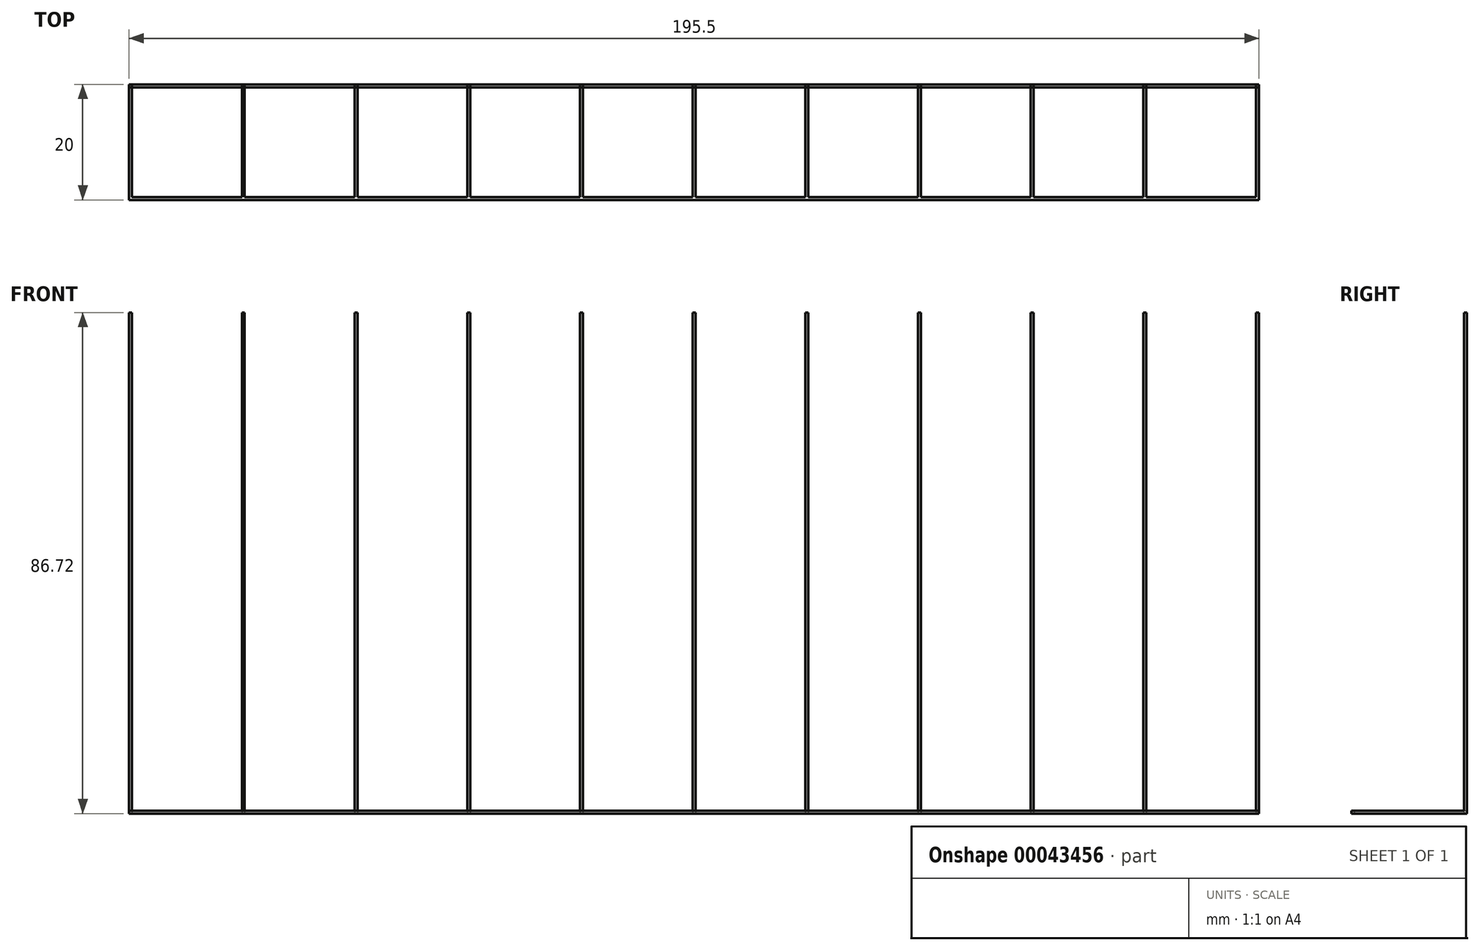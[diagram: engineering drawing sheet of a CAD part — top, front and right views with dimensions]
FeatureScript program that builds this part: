
annotation { "Feature Type Name" : "Feature", "Feature Type Description" : "" }
export const myFeature = defineFeature(function(context is Context, id is Id, definition is map)
    precondition{}
    {
        {
            var Q0;
            Q0=qCreatedBy(makeId("Top.planeOp"),FACE);
            var sketch = newSketch(context, id + "F0", { "sketchPlane" : qUnion([Q0])});
            skLineSegment(sketch, "E0.left", {"start": v(-64.95, 61.53) * mm, "end": v(-64.95, 41.53) * mm});
            skLineSegment(sketch, "E0.right", {"start": v(-44.95, 61.03) * mm, "end": v(-44.95, 42.03) * mm});
            skLineSegment(sketch, "E1.0", {"start": v(-64.45, 61.03) * mm, "end": v(-45.45, 61.03) * mm});
            skLineSegment(sketch, "E1.1", {"start": v(-64.45, 61.03) * mm, "end": v(-64.45, 42.03) * mm});
            skLineSegment(sketch, "E1.2", {"start": v(-64.45, 42.03) * mm, "end": v(-45.45, 42.03) * mm});
            skLineSegment(sketch, "E1.3", {"start": v(-45.45, 61.03) * mm, "end": v(-45.45, 42.03) * mm});
            skLineSegment(sketch, "E2.1.0.1", {"start": v(-44.95, 61.03) * mm, "end": v(-25.95, 61.03) * mm});
            skLineSegment(sketch, "E2.1.0.4", {"start": v(-44.95, 42.03) * mm, "end": v(-25.95, 42.03) * mm});
            skLineSegment(sketch, "E2.1.0.6", {"start": v(-25.95, 61.03) * mm, "end": v(-25.95, 42.03) * mm});
            skLineSegment(sketch, "E2.1.0.7", {"start": v(-25.45, 61.03) * mm, "end": v(-25.45, 42.03) * mm});
            skLineSegment(sketch, "E2.2.0.1", {"start": v(-25.45, 61.03) * mm, "end": v(-6.45, 61.03) * mm});
            skLineSegment(sketch, "E2.2.0.3", {"start": v(-25.45, 61.03) * mm, "end": v(-25.45, 42.03) * mm});
            skLineSegment(sketch, "E2.2.0.4", {"start": v(-25.45, 42.03) * mm, "end": v(-6.45, 42.03) * mm});
            skLineSegment(sketch, "E2.2.0.6", {"start": v(-6.45, 61.03) * mm, "end": v(-6.45, 42.03) * mm});
            skLineSegment(sketch, "E2.2.0.7", {"start": v(-5.95, 61.03) * mm, "end": v(-5.95, 42.03) * mm});
            skLineSegment(sketch, "E2.3.0.1", {"start": v(-5.95, 61.03) * mm, "end": v(13.05, 61.03) * mm});
            skLineSegment(sketch, "E2.3.0.2", {"start": v(-6.45, 61.03) * mm, "end": v(-6.45, 42.03) * mm});
            skLineSegment(sketch, "E2.3.0.3", {"start": v(-5.95, 61.03) * mm, "end": v(-5.95, 42.03) * mm});
            skLineSegment(sketch, "E2.3.0.4", {"start": v(-5.95, 42.03) * mm, "end": v(13.05, 42.03) * mm});
            skLineSegment(sketch, "E2.3.0.6", {"start": v(13.05, 61.03) * mm, "end": v(13.05, 42.03) * mm});
            skLineSegment(sketch, "E2.3.0.7", {"start": v(13.55, 61.03) * mm, "end": v(13.55, 42.03) * mm});
            skLineSegment(sketch, "E2.4.0.1", {"start": v(13.55, 61.03) * mm, "end": v(32.55, 61.03) * mm});
            skLineSegment(sketch, "E2.4.0.2", {"start": v(13.05, 61.03) * mm, "end": v(13.05, 42.03) * mm});
            skLineSegment(sketch, "E2.4.0.3", {"start": v(13.55, 61.03) * mm, "end": v(13.55, 42.03) * mm});
            skLineSegment(sketch, "E2.4.0.4", {"start": v(13.55, 42.03) * mm, "end": v(32.55, 42.03) * mm});
            skLineSegment(sketch, "E2.4.0.6", {"start": v(32.55, 61.03) * mm, "end": v(32.55, 42.03) * mm});
            skLineSegment(sketch, "E2.4.0.7", {"start": v(33.05, 61.03) * mm, "end": v(33.05, 42.03) * mm});
            skLineSegment(sketch, "E2.5.0.1", {"start": v(33.05, 61.03) * mm, "end": v(52.05, 61.03) * mm});
            skLineSegment(sketch, "E2.5.0.2", {"start": v(32.55, 61.03) * mm, "end": v(32.55, 42.03) * mm});
            skLineSegment(sketch, "E2.5.0.3", {"start": v(33.05, 61.03) * mm, "end": v(33.05, 42.03) * mm});
            skLineSegment(sketch, "E2.5.0.4", {"start": v(33.05, 42.03) * mm, "end": v(52.05, 42.03) * mm});
            skLineSegment(sketch, "E2.5.0.6", {"start": v(52.05, 61.03) * mm, "end": v(52.05, 42.03) * mm});
            skLineSegment(sketch, "E2.5.0.7", {"start": v(52.55, 61.03) * mm, "end": v(52.55, 42.03) * mm});
            skLineSegment(sketch, "E2.6.0.1", {"start": v(52.55, 61.03) * mm, "end": v(71.55, 61.03) * mm});
            skLineSegment(sketch, "E2.6.0.3", {"start": v(52.55, 61.03) * mm, "end": v(52.55, 42.03) * mm});
            skLineSegment(sketch, "E2.6.0.4", {"start": v(52.55, 42.03) * mm, "end": v(71.55, 42.03) * mm});
            skLineSegment(sketch, "E2.6.0.6", {"start": v(71.55, 61.03) * mm, "end": v(71.55, 42.03) * mm});
            skLineSegment(sketch, "E2.6.0.7", {"start": v(72.05, 61.03) * mm, "end": v(72.05, 42.03) * mm});
            skLineSegment(sketch, "E2.7.0.1", {"start": v(72.05, 61.03) * mm, "end": v(91.05, 61.03) * mm});
            skLineSegment(sketch, "E2.7.0.2", {"start": v(71.55, 61.03) * mm, "end": v(71.55, 42.03) * mm});
            skLineSegment(sketch, "E2.7.0.3", {"start": v(72.05, 61.03) * mm, "end": v(72.05, 42.03) * mm});
            skLineSegment(sketch, "E2.7.0.4", {"start": v(72.05, 42.03) * mm, "end": v(91.05, 42.03) * mm});
            skLineSegment(sketch, "E2.7.0.6", {"start": v(91.05, 61.03) * mm, "end": v(91.05, 42.03) * mm});
            skLineSegment(sketch, "E2.8.0.1", {"start": v(91.55, 61.03) * mm, "end": v(110.55, 61.03) * mm});
            skLineSegment(sketch, "E2.8.0.2", {"start": v(91.05, 61.03) * mm, "end": v(91.05, 42.03) * mm});
            skLineSegment(sketch, "E2.8.0.3", {"start": v(91.55, 61.03) * mm, "end": v(91.55, 42.03) * mm});
            skLineSegment(sketch, "E2.8.0.4", {"start": v(91.55, 42.03) * mm, "end": v(110.55, 42.03) * mm});
            skLineSegment(sketch, "E2.8.0.6", {"start": v(110.55, 61.03) * mm, "end": v(110.55, 42.03) * mm});
            skLineSegment(sketch, "E2.8.0.7", {"start": v(111.05, 61.03) * mm, "end": v(111.05, 42.03) * mm});
            skLineSegment(sketch, "E2.9.0.1", {"start": v(111.05, 61.03) * mm, "end": v(130.05, 61.03) * mm});
            skLineSegment(sketch, "E2.9.0.2", {"start": v(110.55, 61.03) * mm, "end": v(110.55, 42.03) * mm});
            skLineSegment(sketch, "E2.9.0.3", {"start": v(111.05, 61.03) * mm, "end": v(111.05, 42.03) * mm});
            skLineSegment(sketch, "E2.9.0.4", {"start": v(111.05, 42.03) * mm, "end": v(130.05, 42.03) * mm});
            skLineSegment(sketch, "E2.9.0.6", {"start": v(130.05, 61.03) * mm, "end": v(130.05, 42.03) * mm});
            skLineSegment(sketch, "E2.9.0.7", {"start": v(130.55, 61.53) * mm, "end": v(130.55, 41.53) * mm});
            skPoint(sketch, "E3.orphan", {"position": v(32.55, 61.53) * mm});
            skPoint(sketch, "E4.orphan", {"position": v(13.55, 61.53) * mm});
            skPoint(sketch, "E5.orphan", {"position": v(52.55, 61.53) * mm});
            skPoint(sketch, "E6.orphan", {"position": v(91.55, 41.53) * mm});
            skPoint(sketch, "E7.orphan", {"position": v(71.55, 41.53) * mm});
            skPoint(sketch, "E8.orphan", {"position": v(72.05, 41.53) * mm});
            skPoint(sketch, "E9.orphan", {"position": v(33.05, 41.53) * mm});
            skPoint(sketch, "E10.orphan", {"position": v(-5.95, 41.53) * mm});
            skLineSegment(sketch, "E11", {"start": v(130.55, 61.53) * mm, "end": v(-64.95, 61.53) * mm});
            skLineSegment(sketch, "E12", {"start": v(-64.95, 41.53) * mm, "end": v(130.55, 41.53) * mm});
            skSolve(sketch);
        }
        {
            var Q0;
            Q0=makeQuery(id+"F0.imprint","IMPRINT",FACE,{"disambiguationData":[TD([[makeQuery(id+"F0.imprint","IMPRINT",EDGE,{"derivedFrom":sQuery(id+"F0.wireOp",EDGE,"E0.left")}),1.0]])]});
            extrude(context, id + "F1", {"entities" : qUnion([Q0]), "depth" : 0.5 * mm});
        }
        {
            var Q0;
            Q0=makeQuery(id+"F1.opExtrude","CAP_FACE",FACE,{"disambiguationData":[OSD([sQuery(id+"F0.wireOp",EDGE,"E0.left"),sQuery(id+"F0.wireOp",EDGE,"E1.0"),sQuery(id+"F0.wireOp",EDGE,"E1.1"),sQuery(id+"F0.wireOp",EDGE,"E1.2"),sQuery(id+"F0.wireOp",EDGE,"E2.1.0.1"),sQuery(id+"F0.wireOp",EDGE,"E1.3"),sQuery(id+"F0.wireOp",EDGE,"E0.right"),sQuery(id+"F0.wireOp",EDGE,"E2.1.0.4"),sQuery(id+"F0.wireOp",EDGE,"E2.1.0.6"),sQuery(id+"F0.wireOp",EDGE,"E2.2.0.1"),sQuery(id+"F0.wireOp",EDGE,"E2.2.0.3"),sQuery(id+"F0.wireOp",EDGE,"E2.2.0.4"),sQuery(id+"F0.wireOp",EDGE,"E2.3.0.1"),sQuery(id+"F0.wireOp",EDGE,"E2.3.0.2"),sQuery(id+"F0.wireOp",EDGE,"E2.3.0.3"),sQuery(id+"F0.wireOp",EDGE,"E2.3.0.4"),sQuery(id+"F0.wireOp",EDGE,"E2.4.0.1"),sQuery(id+"F0.wireOp",EDGE,"E2.4.0.2"),sQuery(id+"F0.wireOp",EDGE,"E2.4.0.3"),sQuery(id+"F0.wireOp",EDGE,"E2.4.0.4"),sQuery(id+"F0.wireOp",EDGE,"E2.5.0.1"),sQuery(id+"F0.wireOp",EDGE,"E2.5.0.2"),sQuery(id+"F0.wireOp",EDGE,"E2.5.0.3"),sQuery(id+"F0.wireOp",EDGE,"E2.5.0.4"),sQuery(id+"F0.wireOp",EDGE,"E2.5.0.6"),sQuery(id+"F0.wireOp",EDGE,"E2.6.0.1"),sQuery(id+"F0.wireOp",EDGE,"E2.6.0.3"),sQuery(id+"F0.wireOp",EDGE,"E2.6.0.4"),sQuery(id+"F0.wireOp",EDGE,"E2.7.0.1"),sQuery(id+"F0.wireOp",EDGE,"E2.7.0.2"),sQuery(id+"F0.wireOp",EDGE,"E2.7.0.3"),sQuery(id+"F0.wireOp",EDGE,"E2.7.0.4"),sQuery(id+"F0.wireOp",EDGE,"E2.8.0.1"),sQuery(id+"F0.wireOp",EDGE,"E2.8.0.2"),sQuery(id+"F0.wireOp",EDGE,"E2.8.0.3"),sQuery(id+"F0.wireOp",EDGE,"E2.8.0.4"),sQuery(id+"F0.wireOp",EDGE,"E2.9.0.1"),sQuery(id+"F0.wireOp",EDGE,"E2.9.0.2"),sQuery(id+"F0.wireOp",EDGE,"E2.9.0.3"),sQuery(id+"F0.wireOp",EDGE,"E2.9.0.4"),sQuery(id+"F0.wireOp",EDGE,"E2.9.0.6"),sQuery(id+"F0.wireOp",EDGE,"E2.9.0.7"),sQuery(id+"F0.wireOp",EDGE,"E11"),sQuery(id+"F0.wireOp",EDGE,"E12")])],"isStart":false});
            var sketch = newSketch(context, id + "F2", { "sketchPlane" : qUnion([Q0])});
            skLineSegment(sketch, "E13.bottom", {"start": v(-64.95, 61.53) * mm, "end": v(-64.45, 61.53) * mm});
            skLineSegment(sketch, "E13.top", {"start": v(-64.95, 61.03) * mm, "end": v(-64.45, 61.03) * mm});
            skLineSegment(sketch, "E13.left", {"start": v(-64.95, 61.53) * mm, "end": v(-64.95, 61.03) * mm});
            skLineSegment(sketch, "E13.right", {"start": v(-64.45, 61.53) * mm, "end": v(-64.45, 61.03) * mm});
            skLineSegment(sketch, "E14.bottom", {"start": v(-44.95, 61.03) * mm, "end": v(-45.45, 61.03) * mm});
            skLineSegment(sketch, "E14.top", {"start": v(-44.95, 61.53) * mm, "end": v(-45.45, 61.53) * mm});
            skLineSegment(sketch, "E14.left", {"start": v(-44.95, 61.03) * mm, "end": v(-44.95, 61.53) * mm});
            skLineSegment(sketch, "E14.right", {"start": v(-45.45, 61.03) * mm, "end": v(-45.45, 61.53) * mm});
            skLineSegment(sketch, "E15.bottom", {"start": v(-25.45, 61.03) * mm, "end": v(-25.95, 61.03) * mm});
            skLineSegment(sketch, "E15.top", {"start": v(-25.45, 61.53) * mm, "end": v(-25.95, 61.53) * mm});
            skLineSegment(sketch, "E15.left", {"start": v(-25.45, 61.03) * mm, "end": v(-25.45, 61.53) * mm});
            skLineSegment(sketch, "E15.right", {"start": v(-25.95, 61.03) * mm, "end": v(-25.95, 61.53) * mm});
            skLineSegment(sketch, "E16.bottom", {"start": v(-5.95, 61.03) * mm, "end": v(-6.45, 61.03) * mm});
            skLineSegment(sketch, "E16.top", {"start": v(-5.95, 61.53) * mm, "end": v(-6.45, 61.53) * mm});
            skLineSegment(sketch, "E16.left", {"start": v(-5.95, 61.03) * mm, "end": v(-5.95, 61.53) * mm});
            skLineSegment(sketch, "E16.right", {"start": v(-6.45, 61.03) * mm, "end": v(-6.45, 61.53) * mm});
            skLineSegment(sketch, "E17.bottom", {"start": v(13.55, 61.03) * mm, "end": v(13.05, 61.03) * mm});
            skLineSegment(sketch, "E17.top", {"start": v(13.55, 61.53) * mm, "end": v(13.05, 61.53) * mm});
            skLineSegment(sketch, "E17.left", {"start": v(13.55, 61.03) * mm, "end": v(13.55, 61.53) * mm});
            skLineSegment(sketch, "E17.right", {"start": v(13.05, 61.03) * mm, "end": v(13.05, 61.53) * mm});
            skLineSegment(sketch, "E18.bottom", {"start": v(33.05, 61.03) * mm, "end": v(32.55, 61.03) * mm});
            skLineSegment(sketch, "E18.top", {"start": v(33.05, 61.53) * mm, "end": v(32.55, 61.53) * mm});
            skLineSegment(sketch, "E18.left", {"start": v(33.05, 61.03) * mm, "end": v(33.05, 61.53) * mm});
            skLineSegment(sketch, "E18.right", {"start": v(32.55, 61.03) * mm, "end": v(32.55, 61.53) * mm});
            skLineSegment(sketch, "E19.bottom", {"start": v(52.55, 61.03) * mm, "end": v(52.05, 61.03) * mm});
            skLineSegment(sketch, "E19.top", {"start": v(52.55, 61.53) * mm, "end": v(52.05, 61.53) * mm});
            skLineSegment(sketch, "E19.left", {"start": v(52.55, 61.03) * mm, "end": v(52.55, 61.53) * mm});
            skLineSegment(sketch, "E19.right", {"start": v(52.05, 61.03) * mm, "end": v(52.05, 61.53) * mm});
            skLineSegment(sketch, "E20.bottom", {"start": v(72.05, 61.03) * mm, "end": v(71.55, 61.03) * mm});
            skLineSegment(sketch, "E20.top", {"start": v(72.05, 61.53) * mm, "end": v(71.55, 61.53) * mm});
            skLineSegment(sketch, "E20.left", {"start": v(72.05, 61.03) * mm, "end": v(72.05, 61.53) * mm});
            skLineSegment(sketch, "E20.right", {"start": v(71.55, 61.03) * mm, "end": v(71.55, 61.53) * mm});
            skLineSegment(sketch, "E21.bottom", {"start": v(91.55, 61.03) * mm, "end": v(91.05, 61.03) * mm});
            skLineSegment(sketch, "E21.top", {"start": v(91.55, 61.53) * mm, "end": v(91.05, 61.53) * mm});
            skLineSegment(sketch, "E21.left", {"start": v(91.55, 61.03) * mm, "end": v(91.55, 61.53) * mm});
            skLineSegment(sketch, "E21.right", {"start": v(91.05, 61.03) * mm, "end": v(91.05, 61.53) * mm});
            skLineSegment(sketch, "E22.bottom", {"start": v(111.05, 61.03) * mm, "end": v(110.55, 61.03) * mm});
            skLineSegment(sketch, "E22.top", {"start": v(111.05, 61.53) * mm, "end": v(110.55, 61.53) * mm});
            skLineSegment(sketch, "E22.left", {"start": v(111.05, 61.03) * mm, "end": v(111.05, 61.53) * mm});
            skLineSegment(sketch, "E22.right", {"start": v(110.55, 61.03) * mm, "end": v(110.55, 61.53) * mm});
            skLineSegment(sketch, "E23.bottom", {"start": v(130.05, 61.03) * mm, "end": v(130.55, 61.03) * mm});
            skLineSegment(sketch, "E23.top", {"start": v(130.05, 61.53) * mm, "end": v(130.55, 61.53) * mm});
            skLineSegment(sketch, "E23.left", {"start": v(130.05, 61.03) * mm, "end": v(130.05, 61.53) * mm});
            skLineSegment(sketch, "E23.right", {"start": v(130.55, 61.03) * mm, "end": v(130.55, 61.53) * mm});
            skSolve(sketch);
        }
        {
            var Q0;
            Q0=qSketchRegion(id+"F2",true);
            extrude(context, id + "F3", {"entities" : qUnion([Q0]), "operationType" : NewBodyOperationType.ADD, "depth" : 86.22 * mm});
        }
    });
